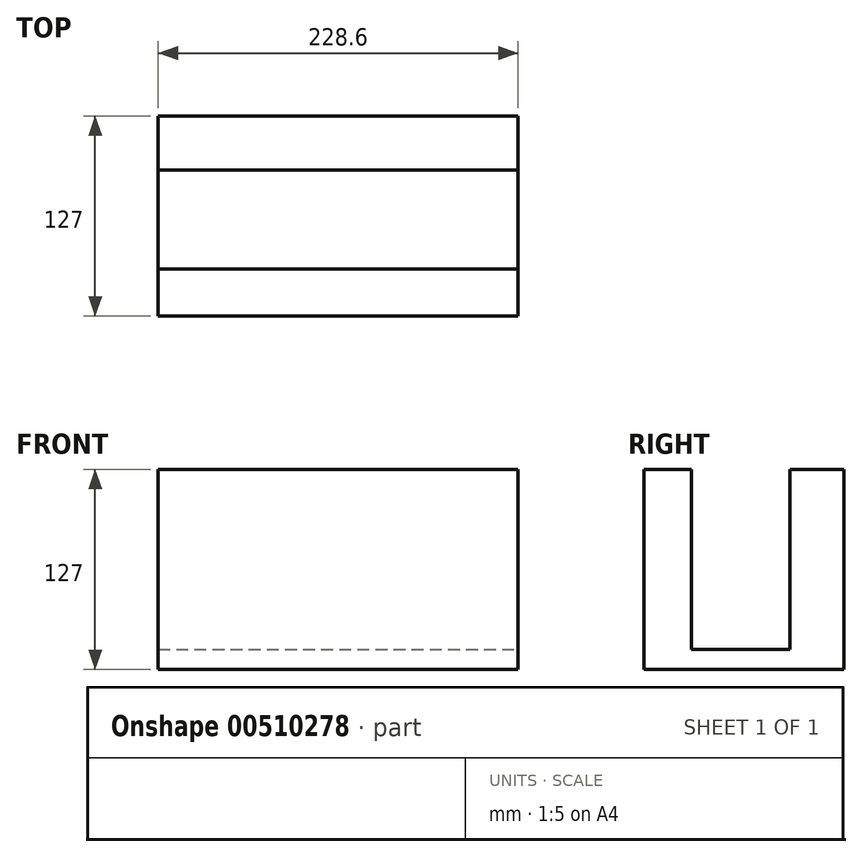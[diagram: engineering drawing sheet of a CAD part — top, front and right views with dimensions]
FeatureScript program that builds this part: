
annotation { "Feature Type Name" : "Feature", "Feature Type Description" : "" }
export const myFeature = defineFeature(function(context is Context, id is Id, definition is map)
    precondition{}
    {
        {
            var Q0;
            Q0=qCreatedBy(makeId("Top.planeOp"),FACE);
            var sketch = newSketch(context, id + "F0", { "sketchPlane" : qUnion([Q0])});
            skLineSegment(sketch, "E0.bottom", {"start": v(114.3, 63.5) * mm, "end": v(-114.3, 63.5) * mm});
            skLineSegment(sketch, "E0.top", {"start": v(114.3, -63.5) * mm, "end": v(-114.3, -63.5) * mm});
            skLineSegment(sketch, "E0.left", {"start": v(114.3, 63.5) * mm, "end": v(114.3, -63.5) * mm});
            skLineSegment(sketch, "E0.right", {"start": v(-114.3, 63.5) * mm, "end": v(-114.3, -63.5) * mm});
            skPoint(sketch, "E0.middle", {"position": v(0, 0) * mm});
            skLineSegment(sketch, "E1", {"start": v(-114.3, 29.16) * mm, "end": v(114.3, 29.16) * mm});
            skLineSegment(sketch, "E2", {"start": v(-114.3, -33.53) * mm, "end": v(114.3, -33.53) * mm});
            skSolve(sketch);
        }
        {
            var Q0;
            {var subQ0=sQuery(id+"F0.wireOp",EDGE,"E1");Q0=makeQuery(id+"F0.imprint","IMPRINT",FACE,{"disambiguationData":[TD([[makeQuery(id+"F0.imprint","IMPRINT",EDGE,{"derivedFrom":subQ0}),-1.0]])]});}
            extrude(context, id + "F1", {"entities" : qUnion([Q0]), "depth" : 12.7 * mm});
        }
        {
            var Q0;
            {var subQ0=sQuery(id+"F0.wireOp",EDGE,"E0.bottom");Q0=makeQuery(id+"F0.imprint","IMPRINT",FACE,{"disambiguationData":[TD([[makeQuery(id+"F0.imprint","IMPRINT",EDGE,{"derivedFrom":subQ0}),1.0]])]});}
            var Q1;
            {var subQ0=sQuery(id+"F0.wireOp",EDGE,"E0.top");Q1=makeQuery(id+"F0.imprint","IMPRINT",FACE,{"disambiguationData":[TD([[makeQuery(id+"F0.imprint","IMPRINT",EDGE,{"derivedFrom":subQ0}),-1.0]])]});}
            extrude(context, id + "F2", {"entities" : qUnion([Q0, Q1]), "operationType" : NewBodyOperationType.ADD, "depth" : 127 * mm});
        }
    });
